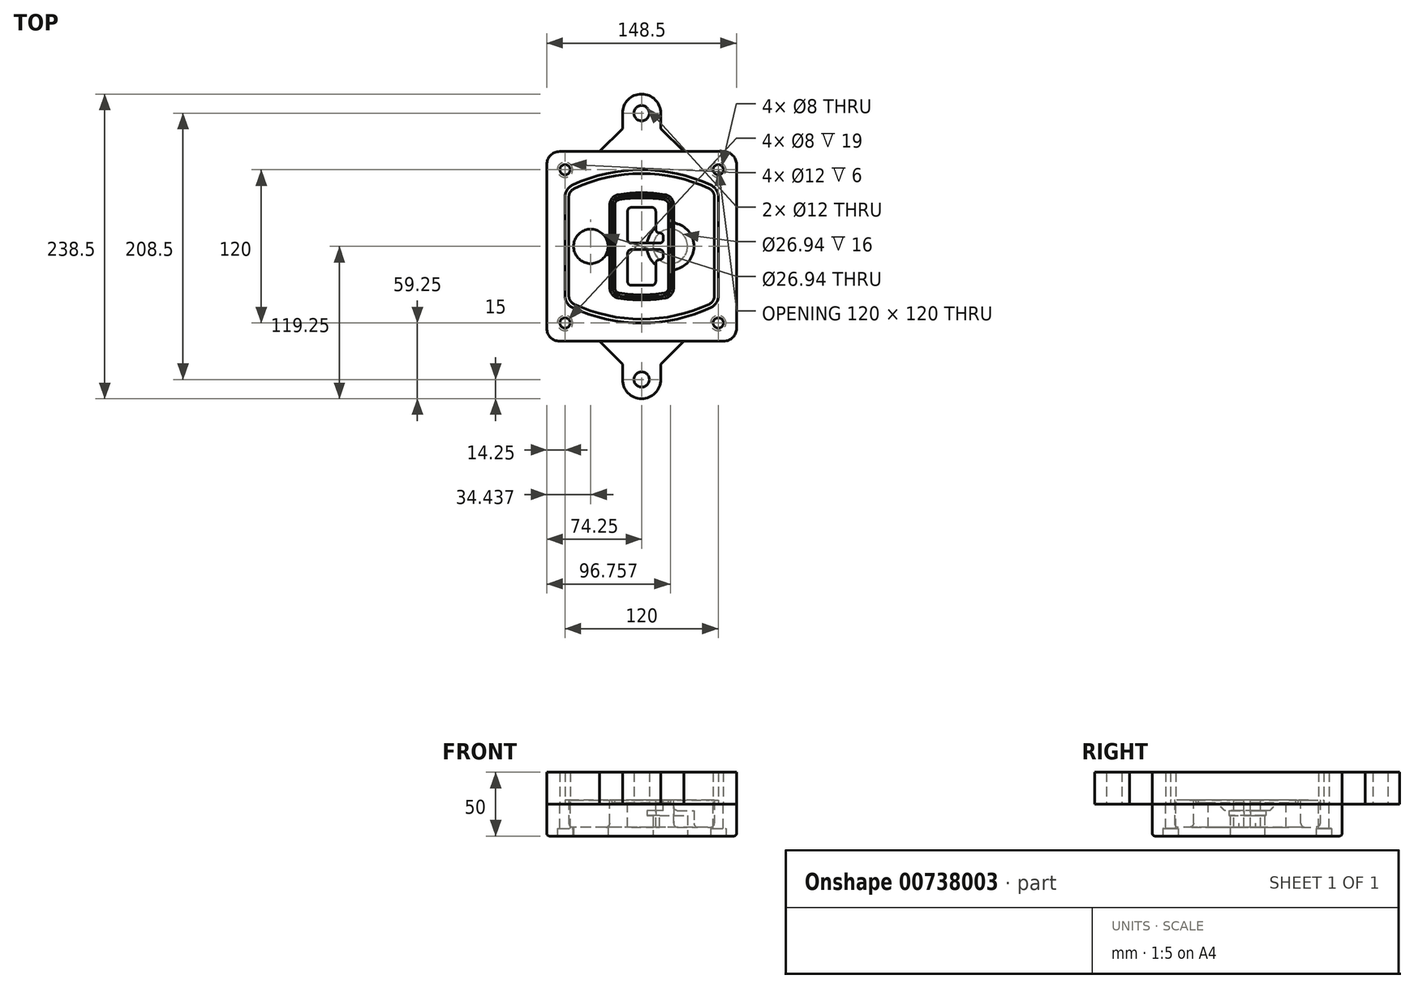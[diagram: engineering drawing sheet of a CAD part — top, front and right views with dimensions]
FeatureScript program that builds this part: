
annotation { "Feature Type Name" : "Feature", "Feature Type Description" : "" }
export const myFeature = defineFeature(function(context is Context, id is Id, definition is map)
    precondition{}
    {
        {
            var Q0;
            Q0=qCreatedBy(makeId("Top.planeOp"),FACE);
            var sketch = newSketch(context, id + "F0", { "sketchPlane" : qUnion([Q0])});
            skPoint(sketch, "E0.rect.middle", {"position": v(0, 0) * mm});
            skLineSegment(sketch, "E1.bottom", {"start": v(-64.25, -74.25) * mm, "end": v(64.25, -74.25) * mm});
            skLineSegment(sketch, "E1.top", {"start": v(-64.25, 74.25) * mm, "end": v(64.25, 74.25) * mm});
            skLineSegment(sketch, "E1.left", {"start": v(-74.25, -64.25) * mm, "end": v(-74.25, 64.25) * mm});
            skLineSegment(sketch, "E1.right", {"start": v(74.25, -64.25) * mm, "end": v(74.25, 64.25) * mm});
            skLineSegment(sketch, "E2", {"start": v(-74.25, 74.25) * mm, "end": v(74.25, -74.25) * mm, "construction": true});
            skLineSegment(sketch, "E3", {"start": v(74.25, 74.25) * mm, "end": v(-74.25, -74.25) * mm, "construction": true});
            skCircle(sketch, "E4", {"center": v(-60, 60) * mm, "radius": 4 * mm});
            skCircle(sketch, "E5", {"center": v(60, 60) * mm, "radius": 4 * mm});
            skCircle(sketch, "E6", {"center": v(60, -60) * mm, "radius": 4 * mm});
            skCircle(sketch, "E7", {"center": v(-60, -60) * mm, "radius": 4 * mm});
            skLineSegment(sketch, "E8", {"start": v(-60, 60) * mm, "end": v(60, 60) * mm, "construction": true});
            skLineSegment(sketch, "E9", {"start": v(60, 60) * mm, "end": v(60, -60) * mm, "construction": true});
            skLineSegment(sketch, "E10", {"start": v(60, -60) * mm, "end": v(-60, -60) * mm, "construction": true});
            skLineSegment(sketch, "E11", {"start": v(-60, -60) * mm, "end": v(-60, 60) * mm, "construction": true});
            skLineSegment(sketch, "E12", {"start": v(-60, 38.83) * mm, "end": v(-60, -38.83) * mm});
            skLineSegment(sketch, "E13", {"start": v(60, 38.83) * mm, "end": v(60, -38.83) * mm});
            skArc(sketch, "E14", {"start": v(54.26, 47.88) * mm, "mid": v(0, 60) * mm, "end": v(-54.26, 47.88) * mm});
            skArc(sketch, "E15", {"start": v(-54.26, -47.88) * mm, "mid": v(0, -60) * mm, "end": v(54.26, -47.88) * mm});
            skLineSegment(sketch, "E16", {"start": v(-60, 0) * mm, "end": v(60, 0) * mm, "construction": true});
            skPoint(sketch, "E17.visualSharp", {"position": v(-60, -45) * mm});
            skArc(sketch, "E17.filletArc", {"start": v(-60, -38.83) * mm, "mid": v(-58.44, -44.2) * mm, "end": v(-54.26, -47.88) * mm});
            skPoint(sketch, "E18.visualSharp", {"position": v(-60, 45) * mm});
            skArc(sketch, "E18.filletArc", {"start": v(-54.26, 47.88) * mm, "mid": v(-58.44, 44.2) * mm, "end": v(-60, 38.83) * mm});
            skPoint(sketch, "E19.visualSharp", {"position": v(60, 45) * mm});
            skArc(sketch, "E19.filletArc", {"start": v(60, 38.83) * mm, "mid": v(58.44, 44.2) * mm, "end": v(54.26, 47.88) * mm});
            skPoint(sketch, "E20.visualSharp", {"position": v(60, -45) * mm});
            skArc(sketch, "E20.filletArc", {"start": v(54.26, -47.88) * mm, "mid": v(58.44, -44.2) * mm, "end": v(60, -38.83) * mm});
            skPoint(sketch, "E21.visualSharp", {"position": v(-74.25, 74.25) * mm});
            skArc(sketch, "E21.filletArc", {"start": v(-64.25, 74.25) * mm, "mid": v(-71.32, 71.32) * mm, "end": v(-74.25, 64.25) * mm});
            skPoint(sketch, "E22.visualSharp", {"position": v(74.25, 74.25) * mm});
            skArc(sketch, "E22.filletArc", {"start": v(74.25, 64.25) * mm, "mid": v(71.32, 71.32) * mm, "end": v(64.25, 74.25) * mm});
            skPoint(sketch, "E23.visualSharp", {"position": v(74.25, -74.25) * mm});
            skArc(sketch, "E23.filletArc", {"start": v(64.25, -74.25) * mm, "mid": v(71.32, -71.32) * mm, "end": v(74.25, -64.25) * mm});
            skPoint(sketch, "E24.visualSharp", {"position": v(-74.25, -74.25) * mm});
            skArc(sketch, "E24.filletArc", {"start": v(-74.25, -64.25) * mm, "mid": v(-71.32, -71.32) * mm, "end": v(-64.25, -74.25) * mm});
            skArc(sketch, "E25.0", {"start": v(57, 38.83) * mm, "mid": v(55.9, 42.58) * mm, "end": v(52.98, 45.17) * mm});
            skLineSegment(sketch, "E25.1", {"start": v(57, 38.83) * mm, "end": v(57, -38.83) * mm});
            skArc(sketch, "E25.2", {"start": v(52.98, -45.17) * mm, "mid": v(55.9, -42.58) * mm, "end": v(57, -38.83) * mm});
            skArc(sketch, "E25.3", {"start": v(-52.98, -45.17) * mm, "mid": v(0, -57) * mm, "end": v(52.98, -45.17) * mm});
            skArc(sketch, "E25.4", {"start": v(-57, -38.83) * mm, "mid": v(-55.9, -42.58) * mm, "end": v(-52.98, -45.17) * mm});
            skArc(sketch, "E25.5", {"start": v(52.98, 45.17) * mm, "mid": v(0, 57) * mm, "end": v(-52.98, 45.17) * mm});
            skLineSegment(sketch, "E25.6", {"start": v(-57, 38.83) * mm, "end": v(-57, -38.83) * mm});
            skArc(sketch, "E25.7", {"start": v(-52.98, 45.17) * mm, "mid": v(-55.9, 42.58) * mm, "end": v(-57, 38.83) * mm});
            skArc(sketch, "E26.0", {"start": v(-55.96, 51.5) * mm, "mid": v(-61.82, 46.33) * mm, "end": v(-64, 38.83) * mm});
            skArc(sketch, "E26.1", {"start": v(55.96, 51.5) * mm, "mid": v(0, 64) * mm, "end": v(-55.96, 51.5) * mm});
            skArc(sketch, "E26.2", {"start": v(64, 38.83) * mm, "mid": v(61.82, 46.33) * mm, "end": v(55.96, 51.5) * mm});
            skLineSegment(sketch, "E26.3", {"start": v(64, 38.83) * mm, "end": v(64, -38.83) * mm});
            skArc(sketch, "E26.4", {"start": v(55.96, -51.5) * mm, "mid": v(61.82, -46.33) * mm, "end": v(64, -38.83) * mm});
            skLineSegment(sketch, "E26.5", {"start": v(-64, 38.83) * mm, "end": v(-64, -38.83) * mm});
            skArc(sketch, "E26.6", {"start": v(-55.96, -51.5) * mm, "mid": v(0, -64) * mm, "end": v(55.96, -51.5) * mm});
            skArc(sketch, "E26.7", {"start": v(-64, -38.83) * mm, "mid": v(-61.82, -46.33) * mm, "end": v(-55.96, -51.5) * mm});
            skSolve(sketch);
        }
        {
            var Q0;
            Q0=makeQuery(id+"F0.imprint","IMPRINT",FACE,{"disambiguationData":[TD([[makeQuery(id+"F0.imprint","IMPRINT",EDGE,{"derivedFrom":sQuery(id+"F0.wireOp",EDGE,"E1.bottom")}),1.0]])]});
            var Q1;
            Q1=makeQuery(id+"F0.imprint","IMPRINT",FACE,{"disambiguationData":[TD([[makeQuery(id+"F0.imprint","IMPRINT",EDGE,{"derivedFrom":sQuery(id+"F0.wireOp",EDGE,"E12")}),1.0]])]});
            var Q2;
            Q2=makeQuery(id+"F0.imprint","IMPRINT",FACE,{"disambiguationData":[TD([[makeQuery(id+"F0.imprint","IMPRINT",EDGE,{"derivedFrom":sQuery(id+"F0.wireOp",EDGE,"E25.0")}),1.0]])]});
            var Q3;
            Q3=makeQuery(id+"F0.imprint","IMPRINT",FACE,{"disambiguationData":[TD([[makeQuery(id+"F0.imprint","IMPRINT",EDGE,{"derivedFrom":sQuery(id+"F0.wireOp",EDGE,"E12")}),-1.0]])]});
            extrude(context, id + "F1", {"entities" : qUnion([Q0, Q1, Q2, Q3]), "oppositeDirection" : true, "depth" : 25 * mm});
        }
        {
            var Q0;
            Q0=makeQuery(id+"F0.imprint","IMPRINT",FACE,{"disambiguationData":[TD([[makeQuery(id+"F0.imprint","IMPRINT",EDGE,{"derivedFrom":sQuery(id+"F0.wireOp",EDGE,"E12")}),1.0]])]});
            extrude(context, id + "F2", {"entities" : qUnion([Q0]), "operationType" : NewBodyOperationType.ADD, "depth" : 3 * mm});
        }
        {
            var Q0;
            Q0=makeQuery(id+"F0.imprint","IMPRINT",FACE,{"disambiguationData":[TD([[makeQuery(id+"F0.imprint","IMPRINT",EDGE,{"derivedFrom":sQuery(id+"F0.wireOp",EDGE,"E25.0")}),1.0]])]});
            extrude(context, id + "F3", {"entities" : qUnion([Q0]), "operationType" : NewBodyOperationType.REMOVE, "oppositeDirection" : true, "depth" : 18 * mm});
        }
        {
            var Q0;
            Q0=makeQuery(id+"F2.opExtrude","CAP_FACE",FACE,{"disambiguationData":[OSD([sQuery(id+"F0.wireOp",EDGE,"E12"),sQuery(id+"F0.wireOp",EDGE,"E13"),sQuery(id+"F0.wireOp",EDGE,"E14"),sQuery(id+"F0.wireOp",EDGE,"E15"),sQuery(id+"F0.wireOp",EDGE,"E17.filletArc"),sQuery(id+"F0.wireOp",EDGE,"E18.filletArc"),sQuery(id+"F0.wireOp",EDGE,"E19.filletArc"),sQuery(id+"F0.wireOp",EDGE,"E20.filletArc"),sQuery(id+"F0.wireOp",EDGE,"E25.0"),sQuery(id+"F0.wireOp",EDGE,"E25.1"),sQuery(id+"F0.wireOp",EDGE,"E25.2"),sQuery(id+"F0.wireOp",EDGE,"E25.3"),sQuery(id+"F0.wireOp",EDGE,"E25.4"),sQuery(id+"F0.wireOp",EDGE,"E25.5"),sQuery(id+"F0.wireOp",EDGE,"E25.6"),sQuery(id+"F0.wireOp",EDGE,"E25.7")])],"isStart":false});
            var sketch = newSketch(context, id + "F4", { "sketchPlane" : qUnion([Q0])});
            skArc(sketch, "E27.0", {"start": v(-18.34, -40.45) * mm, "mid": v(0, -42) * mm, "end": v(18.34, -40.45) * mm});
            skArc(sketch, "E28.0", {"start": v(18.34, 40.45) * mm, "mid": v(0, 42) * mm, "end": v(-18.34, 40.45) * mm});
            skLineSegment(sketch, "E29", {"start": v(-25, 32.57) * mm, "end": v(-25, -32.57) * mm});
            skLineSegment(sketch, "E30", {"start": v(25, 32.57) * mm, "end": v(25, -32.57) * mm});
            skLineSegment(sketch, "E31", {"start": v(-25, 39.1) * mm, "end": v(25, 39.1) * mm, "construction": true});
            skLineSegment(sketch, "E32", {"start": v(-25, -39.1) * mm, "end": v(25, -39.1) * mm, "construction": true});
            skPoint(sketch, "E33.visualSharp", {"position": v(-25, 39.1) * mm});
            skArc(sketch, "E33.filletArc", {"start": v(-18.34, 40.45) * mm, "mid": v(-23.11, 37.73) * mm, "end": v(-25, 32.57) * mm});
            skPoint(sketch, "E34.visualSharp", {"position": v(25, 39.1) * mm});
            skArc(sketch, "E34.filletArc", {"start": v(25, 32.57) * mm, "mid": v(23.11, 37.73) * mm, "end": v(18.34, 40.45) * mm});
            skPoint(sketch, "E35.visualSharp", {"position": v(25, -39.1) * mm});
            skArc(sketch, "E35.filletArc", {"start": v(18.34, -40.45) * mm, "mid": v(23.11, -37.73) * mm, "end": v(25, -32.57) * mm});
            skPoint(sketch, "E36.visualSharp", {"position": v(-25, -39.1) * mm});
            skArc(sketch, "E36.filletArc", {"start": v(-25, -32.57) * mm, "mid": v(-23.11, -37.73) * mm, "end": v(-18.34, -40.45) * mm});
            skArc(sketch, "E37.0", {"start": v(52.98, 45.17) * mm, "mid": v(0, 57) * mm, "end": v(-52.98, 45.17) * mm});
            skArc(sketch, "E37.1", {"start": v(-52.98, 45.17) * mm, "mid": v(-55.9, 42.58) * mm, "end": v(-57, 38.83) * mm});
            skLineSegment(sketch, "E37.2", {"start": v(-57, 38.83) * mm, "end": v(-57, -38.83) * mm});
            skArc(sketch, "E37.3", {"start": v(-57, -38.83) * mm, "mid": v(-55.9, -42.58) * mm, "end": v(-52.98, -45.17) * mm});
            skArc(sketch, "E37.4", {"start": v(-52.98, -45.17) * mm, "mid": v(0, -57) * mm, "end": v(52.98, -45.17) * mm});
            skArc(sketch, "E37.5", {"start": v(52.98, -45.17) * mm, "mid": v(55.9, -42.58) * mm, "end": v(57, -38.83) * mm});
            skLineSegment(sketch, "E37.6", {"start": v(57, 38.83) * mm, "end": v(57, -38.83) * mm});
            skArc(sketch, "E37.7", {"start": v(57, 38.83) * mm, "mid": v(55.9, 42.58) * mm, "end": v(52.98, 45.17) * mm});
            skLineSegment(sketch, "E38.0", {"start": v(23, 32.57) * mm, "end": v(23, -32.57) * mm});
            skArc(sketch, "E38.1", {"start": v(18, -38.48) * mm, "mid": v(21.58, -36.44) * mm, "end": v(23, -32.57) * mm});
            skArc(sketch, "E38.2", {"start": v(-18, -38.48) * mm, "mid": v(0, -40) * mm, "end": v(18, -38.48) * mm});
            skArc(sketch, "E38.3", {"start": v(-23, -32.57) * mm, "mid": v(-21.58, -36.44) * mm, "end": v(-18, -38.48) * mm});
            skLineSegment(sketch, "E38.4", {"start": v(-23, 32.57) * mm, "end": v(-23, -32.57) * mm});
            skArc(sketch, "E38.5", {"start": v(23, 32.57) * mm, "mid": v(21.58, 36.44) * mm, "end": v(18, 38.48) * mm});
            skArc(sketch, "E38.6", {"start": v(-18, 38.48) * mm, "mid": v(-21.58, 36.44) * mm, "end": v(-23, 32.57) * mm});
            skArc(sketch, "E38.7", {"start": v(18, 38.48) * mm, "mid": v(0, 40) * mm, "end": v(-18, 38.48) * mm});
            skArc(sketch, "E39.0", {"start": v(21, 32.57) * mm, "mid": v(20.06, 35.15) * mm, "end": v(17.67, 36.5) * mm});
            skLineSegment(sketch, "E39.1", {"start": v(21, 32.57) * mm, "end": v(21, -32.57) * mm});
            skArc(sketch, "E39.2", {"start": v(17.67, -36.5) * mm, "mid": v(20.06, -35.15) * mm, "end": v(21, -32.57) * mm});
            skArc(sketch, "E39.3", {"start": v(-17.67, -36.5) * mm, "mid": v(0, -38) * mm, "end": v(17.67, -36.5) * mm});
            skArc(sketch, "E39.4", {"start": v(-21, -32.57) * mm, "mid": v(-20.06, -35.15) * mm, "end": v(-17.67, -36.5) * mm});
            skArc(sketch, "E39.5", {"start": v(17.67, 36.5) * mm, "mid": v(0, 38) * mm, "end": v(-17.67, 36.5) * mm});
            skLineSegment(sketch, "E39.6", {"start": v(-21, 32.57) * mm, "end": v(-21, -32.57) * mm});
            skArc(sketch, "E39.7", {"start": v(-17.67, 36.5) * mm, "mid": v(-20.06, 35.15) * mm, "end": v(-21, 32.57) * mm});
            skLineSegment(sketch, "E40", {"start": v(-25, 0) * mm, "end": v(25, 0) * mm, "construction": true});
            skLineSegment(sketch, "E41", {"start": v(-11, 5.5) * mm, "end": v(-11, 27.5) * mm});
            skLineSegment(sketch, "E42", {"start": v(-8, 30.5) * mm, "end": v(8, 30.5) * mm});
            skLineSegment(sketch, "E43", {"start": v(11, 27.5) * mm, "end": v(11, 13.5) * mm});
            skLineSegment(sketch, "E44", {"start": v(14, 10.5) * mm, "end": v(14, 10.5) * mm});
            skLineSegment(sketch, "E45", {"start": v(17, 7.5) * mm, "end": v(17, 5.5) * mm});
            skLineSegment(sketch, "E46", {"start": v(14, 2.5) * mm, "end": v(-8, 2.5) * mm});
            skPoint(sketch, "E47.visualSharp", {"position": v(-11, 30.5) * mm});
            skArc(sketch, "E47.filletArc", {"start": v(-8, 30.5) * mm, "mid": v(-10.12, 29.62) * mm, "end": v(-11, 27.5) * mm});
            skPoint(sketch, "E48.visualSharp", {"position": v(11, 30.5) * mm});
            skArc(sketch, "E48.filletArc", {"start": v(11, 27.5) * mm, "mid": v(10.12, 29.62) * mm, "end": v(8, 30.5) * mm});
            skPoint(sketch, "E49.visualSharp", {"position": v(11, 10.5) * mm});
            skArc(sketch, "E49.filletArc", {"start": v(11, 13.5) * mm, "mid": v(11.88, 11.38) * mm, "end": v(14, 10.5) * mm});
            skPoint(sketch, "E50.visualSharp", {"position": v(17, 10.5) * mm});
            skArc(sketch, "E50.filletArc", {"start": v(17, 7.5) * mm, "mid": v(16.12, 9.62) * mm, "end": v(14, 10.5) * mm});
            skPoint(sketch, "E51.visualSharp", {"position": v(17, 2.5) * mm});
            skArc(sketch, "E51.filletArc", {"start": v(14, 2.5) * mm, "mid": v(16.12, 3.38) * mm, "end": v(17, 5.5) * mm});
            skPoint(sketch, "E52.visualSharp", {"position": v(-11, 2.5) * mm});
            skArc(sketch, "E52.filletArc", {"start": v(-11, 5.5) * mm, "mid": v(-10.12, 3.38) * mm, "end": v(-8, 2.5) * mm});
            skLineSegment(sketch, "E53.0.MirrorCS", {"start": v(14, -2.5) * mm, "end": v(-8, -2.5) * mm});
            skArc(sketch, "E54.0.MirrorCS", {"start": v(-11, -5.5) * mm, "mid": v(-10.12, -3.38) * mm, "end": v(-8, -2.5) * mm});
            skLineSegment(sketch, "E55.0.MirrorCS", {"start": v(-11, -5.5) * mm, "end": v(-11, -27.5) * mm});
            skArc(sketch, "E56.0.MirrorCS", {"start": v(-8, -30.5) * mm, "mid": v(-10.12, -29.62) * mm, "end": v(-11, -27.5) * mm});
            skLineSegment(sketch, "E57.0.MirrorCS", {"start": v(-8, -30.5) * mm, "end": v(8, -30.5) * mm});
            skArc(sketch, "E58.0.MirrorCS", {"start": v(11, -27.5) * mm, "mid": v(10.12, -29.62) * mm, "end": v(8, -30.5) * mm});
            skLineSegment(sketch, "E59.0.MirrorCS", {"start": v(11, -27.5) * mm, "end": v(11, -13.5) * mm});
            skArc(sketch, "E60.0.MirrorCS", {"start": v(11, -13.5) * mm, "mid": v(11.88, -11.38) * mm, "end": v(14, -10.5) * mm});
            skArc(sketch, "E61.0.MirrorCS", {"start": v(17, -7.5) * mm, "mid": v(16.12, -9.62) * mm, "end": v(14, -10.5) * mm});
            skLineSegment(sketch, "E62.0.MirrorCS", {"start": v(17, -7.5) * mm, "end": v(17, -5.5) * mm});
            skArc(sketch, "E63.0.MirrorCS", {"start": v(14, -2.5) * mm, "mid": v(16.12, -3.38) * mm, "end": v(17, -5.5) * mm});
            skSolve(sketch);
        }
        {
            var Q0;
            Q0=makeQuery(id+"F4.imprint","IMPRINT",FACE,{"disambiguationData":[TD([[makeQuery(id+"F4.imprint","IMPRINT",EDGE,{"derivedFrom":sQuery(id+"F4.wireOp",EDGE,"E27.0")}),1.0]])]});
            var Q1;
            Q1=makeQuery(id+"F4.imprint","IMPRINT",FACE,{"disambiguationData":[TD([[makeQuery(id+"F4.imprint","IMPRINT",EDGE,{"derivedFrom":sQuery(id+"F4.wireOp",EDGE,"E38.0")}),-1.0]])]});
            var Q2;
            Q2=makeQuery(id+"F4.imprint","IMPRINT",FACE,{"disambiguationData":[TD([[makeQuery(id+"F4.imprint","IMPRINT",EDGE,{"derivedFrom":sQuery(id+"F4.wireOp",EDGE,"E39.0")}),1.0]])]});
            extrude(context, id + "F5", {"entities" : qUnion([Q0, Q1, Q2]), "operationType" : NewBodyOperationType.ADD, "endBound" : BoundingType.UP_TO_NEXT, "oppositeDirection" : true, "depth" : 25 * mm});
        }
        {
            var Q0;
            Q0=makeQuery(id+"F4.imprint","IMPRINT",FACE,{"disambiguationData":[TD([[makeQuery(id+"F4.imprint","IMPRINT",EDGE,{"derivedFrom":sQuery(id+"F4.wireOp",EDGE,"E38.0")}),-1.0]])]});
            extrude(context, id + "F6", {"entities" : qUnion([Q0]), "operationType" : NewBodyOperationType.REMOVE, "oppositeDirection" : true, "depth" : 2 * mm});
        }
        {
            var Q0;
            Q0=makeQuery(id+"F1.opExtrude","CAP_FACE",FACE,{"disambiguationData":[OSD([sQuery(id+"F0.wireOp",EDGE,"E1.bottom"),sQuery(id+"F0.wireOp",EDGE,"E1.top"),sQuery(id+"F0.wireOp",EDGE,"E1.left"),sQuery(id+"F0.wireOp",EDGE,"E1.right"),sQuery(id+"F0.wireOp",EDGE,"E4"),sQuery(id+"F0.wireOp",EDGE,"E5"),sQuery(id+"F0.wireOp",EDGE,"E6"),sQuery(id+"F0.wireOp",EDGE,"E7"),sQuery(id+"F0.wireOp",EDGE,"E21.filletArc"),sQuery(id+"F0.wireOp",EDGE,"E22.filletArc"),sQuery(id+"F0.wireOp",EDGE,"E23.filletArc"),sQuery(id+"F0.wireOp",EDGE,"E24.filletArc")])],"isStart":false});
            var sketch = newSketch(context, id + "F7", { "sketchPlane" : qUnion([Q0])});
            skCircle(sketch, "E64", {"center": v(22.5, 0) * mm, "radius": 13.47 * mm});
            skCircle(sketch, "E65", {"center": v(-39.81, 0) * mm, "radius": 13.47 * mm});
            skLineSegment(sketch, "E66", {"start": v(74.25, 0) * mm, "end": v(-74.25, 0) * mm});
            skCircle(sketch, "E67", {"center": v(22.5, 0) * mm, "radius": 18.47 * mm});
            skCircle(sketch, "E68", {"center": v(60, -60) * mm, "radius": 6 * mm});
            skCircle(sketch, "E69", {"center": v(-60, -60) * mm, "radius": 6 * mm});
            skCircle(sketch, "E70", {"center": v(-60, 60) * mm, "radius": 6 * mm});
            skCircle(sketch, "E71", {"center": v(60, 60) * mm, "radius": 6 * mm});
            skSolve(sketch);
        }
        {
            var Q0;
            {var subQ1=sQuery(id+"F7.wireOp",EDGE,"E66");var subQ4=sQuery(id+"F7.wireOp",EDGE,"E64");var subQ6=makeQuery(id+"F7.imprint","INTERSECT",VERTEX,{"disambiguationData":[OD(0.0)],"derivedFrom":[subQ4,subQ1]});Q0=makeQuery(id+"F7.imprint","IMPRINT",FACE,{"disambiguationData":[TD([[makeQuery(id+"F7.imprint","IMPRINT",EDGE,{"disambiguationData":[TD([[subQ6,-1.0]])],"derivedFrom":subQ4}),-1.0]])]});}
            var Q1;
            {var subQ0=sQuery(id+"F7.wireOp",EDGE,"E66");var subQ1=sQuery(id+"F7.wireOp",EDGE,"E64");var subQ3=makeQuery(id+"F7.imprint","INTERSECT",VERTEX,{"disambiguationData":[OD(0.0)],"derivedFrom":[subQ1,subQ0]});Q1=makeQuery(id+"F7.imprint","IMPRINT",FACE,{"disambiguationData":[TD([[makeQuery(id+"F7.imprint","IMPRINT",EDGE,{"disambiguationData":[TD([[subQ3,-1.0]])],"derivedFrom":subQ1}),1.0]])]});}
            var Q2;
            {var subQ0=sQuery(id+"F7.wireOp",EDGE,"E66");var subQ1=sQuery(id+"F7.wireOp",EDGE,"E64");var subQ3=makeQuery(id+"F7.imprint","INTERSECT",VERTEX,{"disambiguationData":[OD(0.0)],"derivedFrom":[subQ1,subQ0]});Q2=makeQuery(id+"F7.imprint","IMPRINT",FACE,{"disambiguationData":[TD([[makeQuery(id+"F7.imprint","IMPRINT",EDGE,{"disambiguationData":[TD([[subQ3,1.0]])],"derivedFrom":subQ1}),1.0]])]});}
            var Q3;
            {var subQ1=sQuery(id+"F7.wireOp",EDGE,"E66");var subQ4=sQuery(id+"F7.wireOp",EDGE,"E64");var subQ6=makeQuery(id+"F7.imprint","INTERSECT",VERTEX,{"disambiguationData":[OD(0.0)],"derivedFrom":[subQ4,subQ1]});Q3=makeQuery(id+"F7.imprint","IMPRINT",FACE,{"disambiguationData":[TD([[makeQuery(id+"F7.imprint","IMPRINT",EDGE,{"disambiguationData":[TD([[subQ6,1.0]])],"derivedFrom":subQ4}),-1.0]])]});}
            extrude(context, id + "F8", {"entities" : qUnion([Q0, Q1, Q2, Q3]), "operationType" : NewBodyOperationType.ADD, "oppositeDirection" : true, "depth" : 20 * mm});
        }
        {
            var Q0;
            {var subQ0=sQuery(id+"F7.wireOp",EDGE,"E66");var subQ1=sQuery(id+"F7.wireOp",EDGE,"E64");var subQ3=makeQuery(id+"F7.imprint","INTERSECT",VERTEX,{"disambiguationData":[OD(0.0)],"derivedFrom":[subQ1,subQ0]});Q0=makeQuery(id+"F7.imprint","IMPRINT",FACE,{"disambiguationData":[TD([[makeQuery(id+"F7.imprint","IMPRINT",EDGE,{"disambiguationData":[TD([[subQ3,-1.0]])],"derivedFrom":subQ1}),1.0]])]});}
            var Q1;
            {var subQ0=sQuery(id+"F7.wireOp",EDGE,"E66");var subQ1=sQuery(id+"F7.wireOp",EDGE,"E64");var subQ3=makeQuery(id+"F7.imprint","INTERSECT",VERTEX,{"disambiguationData":[OD(0.0)],"derivedFrom":[subQ1,subQ0]});Q1=makeQuery(id+"F7.imprint","IMPRINT",FACE,{"disambiguationData":[TD([[makeQuery(id+"F7.imprint","IMPRINT",EDGE,{"disambiguationData":[TD([[subQ3,1.0]])],"derivedFrom":subQ1}),1.0]])]});}
            extrude(context, id + "F9", {"entities" : qUnion([Q0, Q1]), "operationType" : NewBodyOperationType.REMOVE, "oppositeDirection" : true, "depth" : 16 * mm});
        }
        {
            var Q0;
            {var subQ0=sQuery(id+"F7.wireOp",EDGE,"E66");var subQ1=sQuery(id+"F7.wireOp",EDGE,"E65");var subQ3=makeQuery(id+"F7.imprint","INTERSECT",VERTEX,{"disambiguationData":[OD(0.0)],"derivedFrom":[subQ1,subQ0]});Q0=makeQuery(id+"F7.imprint","IMPRINT",FACE,{"disambiguationData":[TD([[makeQuery(id+"F7.imprint","IMPRINT",EDGE,{"disambiguationData":[TD([[subQ3,-1.0]])],"derivedFrom":subQ1}),1.0]])]});}
            var Q1;
            {var subQ0=sQuery(id+"F7.wireOp",EDGE,"E66");var subQ1=sQuery(id+"F7.wireOp",EDGE,"E65");var subQ3=makeQuery(id+"F7.imprint","INTERSECT",VERTEX,{"disambiguationData":[OD(0.0)],"derivedFrom":[subQ1,subQ0]});Q1=makeQuery(id+"F7.imprint","IMPRINT",FACE,{"disambiguationData":[TD([[makeQuery(id+"F7.imprint","IMPRINT",EDGE,{"disambiguationData":[TD([[subQ3,1.0]])],"derivedFrom":subQ1}),1.0]])]});}
            extrude(context, id + "F10", {"entities" : qUnion([Q0, Q1]), "operationType" : NewBodyOperationType.REMOVE, "oppositeDirection" : true, "depth" : 25 * mm});
        }
        {
            var Q0;
            Q0=makeQuery(id+"F7.imprint","IMPRINT",FACE,{"disambiguationData":[TD([[makeQuery(id+"F7.imprint","IMPRINT",EDGE,{"derivedFrom":sQuery(id+"F7.wireOp",EDGE,"E68")}),1.0]])]});
            var Q1;
            Q1=makeQuery(id+"F7.imprint","IMPRINT",FACE,{"disambiguationData":[TD([[makeQuery(id+"F7.imprint","IMPRINT",EDGE,{"derivedFrom":makeQuery(id+"F1.opExtrude","CAP_EDGE",EDGE,{"disambiguationData":[OSD([sQuery(id+"F0.wireOp",EDGE,"E5")])],"isStart":false})}),-1.0]])]});
            var Q2;
            Q2=makeQuery(id+"F7.imprint","IMPRINT",FACE,{"disambiguationData":[TD([[makeQuery(id+"F7.imprint","IMPRINT",EDGE,{"derivedFrom":sQuery(id+"F7.wireOp",EDGE,"E69")}),1.0]])]});
            var Q3;
            Q3=makeQuery(id+"F7.imprint","IMPRINT",FACE,{"disambiguationData":[TD([[makeQuery(id+"F7.imprint","IMPRINT",EDGE,{"derivedFrom":makeQuery(id+"F1.opExtrude","CAP_EDGE",EDGE,{"disambiguationData":[OSD([sQuery(id+"F0.wireOp",EDGE,"E4")])],"isStart":false})}),-1.0]])]});
            var Q4;
            Q4=makeQuery(id+"F7.imprint","IMPRINT",FACE,{"disambiguationData":[TD([[makeQuery(id+"F7.imprint","IMPRINT",EDGE,{"derivedFrom":sQuery(id+"F7.wireOp",EDGE,"E70")}),1.0]])]});
            var Q5;
            Q5=makeQuery(id+"F7.imprint","IMPRINT",FACE,{"disambiguationData":[TD([[makeQuery(id+"F7.imprint","IMPRINT",EDGE,{"derivedFrom":makeQuery(id+"F1.opExtrude","CAP_EDGE",EDGE,{"disambiguationData":[OSD([sQuery(id+"F0.wireOp",EDGE,"E7")])],"isStart":false})}),-1.0]])]});
            var Q6;
            Q6=makeQuery(id+"F7.imprint","IMPRINT",FACE,{"disambiguationData":[TD([[makeQuery(id+"F7.imprint","IMPRINT",EDGE,{"derivedFrom":sQuery(id+"F7.wireOp",EDGE,"E71")}),1.0]])]});
            var Q7;
            Q7=makeQuery(id+"F7.imprint","IMPRINT",FACE,{"disambiguationData":[TD([[makeQuery(id+"F7.imprint","IMPRINT",EDGE,{"derivedFrom":makeQuery(id+"F1.opExtrude","CAP_EDGE",EDGE,{"disambiguationData":[OSD([sQuery(id+"F0.wireOp",EDGE,"E6")])],"isStart":false})}),-1.0]])]});
            extrude(context, id + "F11", {"entities" : qUnion([Q0, Q1, Q2, Q3, Q4, Q5, Q6, Q7]), "operationType" : NewBodyOperationType.REMOVE, "oppositeDirection" : true, "depth" : 6 * mm});
        }
        {
            var Q0;
            Q0=makeQuery(id+"F9.boolean.opBoolean","COPY",FACE,{"derivedFrom":makeQuery(id+"F9.opExtrude","CAP_FACE",FACE,{"disambiguationData":[OSD([sQuery(id+"F7.wireOp",EDGE,"E64")])],"isStart":false})});
            var sketch = newSketch(context, id + "F12", { "sketchPlane" : qUnion([Q0])});
            skArc(sketch, "E72.0", {"start": v(11, 14.45) * mm, "mid": v(6.45, 9.13) * mm, "end": v(4.2, 2.5) * mm});
            skArc(sketch, "E72.1", {"start": v(4.2, -2.5) * mm, "mid": v(6.45, -9.13) * mm, "end": v(11, -14.45) * mm});
            skLineSegment(sketch, "E73", {"start": v(4.2, -2.5) * mm, "end": v(14, -2.5) * mm});
            skLineSegment(sketch, "E74.0", {"start": v(14, 2.5) * mm, "end": v(4.2, 2.5) * mm});
            skArc(sketch, "E74.1", {"start": v(14, 2.5) * mm, "mid": v(16.12, 3.38) * mm, "end": v(17, 5.5) * mm});
            skLineSegment(sketch, "E74.2", {"start": v(17, 7.5) * mm, "end": v(17, 5.5) * mm});
            skArc(sketch, "E74.3", {"start": v(17, 7.5) * mm, "mid": v(16.12, 9.62) * mm, "end": v(14, 10.5) * mm});
            skArc(sketch, "E74.4", {"start": v(11, 13.5) * mm, "mid": v(11.88, 11.38) * mm, "end": v(14, 10.5) * mm});
            skLineSegment(sketch, "E74.5", {"start": v(11, 14.45) * mm, "end": v(11, 13.5) * mm});
            skLineSegment(sketch, "E74.7", {"start": v(14, -2.5) * mm, "end": v(4.2, -2.5) * mm});
            skArc(sketch, "E74.8", {"start": v(14, -2.5) * mm, "mid": v(16.12, -3.38) * mm, "end": v(17, -5.5) * mm});
            skLineSegment(sketch, "E74.9", {"start": v(17, -7.5) * mm, "end": v(17, -5.5) * mm});
            skArc(sketch, "E74.10", {"start": v(17, -7.5) * mm, "mid": v(16.12, -9.62) * mm, "end": v(14, -10.5) * mm});
            skArc(sketch, "E74.11", {"start": v(11, -13.5) * mm, "mid": v(11.88, -11.38) * mm, "end": v(14, -10.5) * mm});
            skLineSegment(sketch, "E74.12", {"start": v(11, -14.45) * mm, "end": v(11, -13.5) * mm});
            skPoint(sketch, "E75.orphan", {"position": v(11, -27.5) * mm});
            skPoint(sketch, "E76.orphan", {"position": v(-8, -2.5) * mm});
            skPoint(sketch, "E77.orphan", {"position": v(-8, 2.5) * mm});
            skPoint(sketch, "E78.orphan", {"position": v(11, 27.5) * mm});
            skSolve(sketch);
        }
        {
            var Q0;
            {var subQ7=sQuery(id+"F12.wireOp",EDGE,"E72.0");var subQ14=sQuery(id+"F12.wireOp",EDGE,"E72.1");var subQ16=sQuery(id+"F12.wireOp",EDGE,"E74.1");var subQ18=sQuery(id+"F12.wireOp",EDGE,"E74.8");Q0=qUnion([makeQuery(id+"F12.imprint","IMPRINT",FACE,{"disambiguationData":[TD([[makeQuery(id+"F12.imprint","IMPRINT",EDGE,{"derivedFrom":subQ7}),1.0]])]}),makeQuery(id+"F12.imprint","IMPRINT",FACE,{"disambiguationData":[TD([[makeQuery(id+"F12.imprint","IMPRINT",EDGE,{"derivedFrom":subQ14}),1.0]])]}),makeQuery(id+"F12.imprint","IMPRINT",FACE,{"disambiguationData":[TD([[makeQuery(id+"F12.imprint","IMPRINT",EDGE,{"derivedFrom":subQ16}),1.0]])]}),makeQuery(id+"F12.imprint","IMPRINT",FACE,{"disambiguationData":[TD([[makeQuery(id+"F12.imprint","IMPRINT",EDGE,{"derivedFrom":subQ18}),-1.0]])]})]);}
            var Q1;
            Q1=makeQuery(id+"F5.boolean.opBoolean","SPLIT",FACE,{"disambiguationData":[TD([makeQuery(id+"F5.opExtrude","SWEPT_FACE",FACE,{"disambiguationData":[OSD([sQuery(id+"F4.wireOp",EDGE,"E41")])]})])],"derivedFrom":makeQuery(id+"F3.boolean.opBoolean","COPY",FACE,{"derivedFrom":makeQuery(id+"F3.opExtrude","CAP_FACE",FACE,{"disambiguationData":[OSD([sQuery(id+"F0.wireOp",EDGE,"E25.0"),sQuery(id+"F0.wireOp",EDGE,"E25.1"),sQuery(id+"F0.wireOp",EDGE,"E25.2"),sQuery(id+"F0.wireOp",EDGE,"E25.3"),sQuery(id+"F0.wireOp",EDGE,"E25.4"),sQuery(id+"F0.wireOp",EDGE,"E25.5"),sQuery(id+"F0.wireOp",EDGE,"E25.6"),sQuery(id+"F0.wireOp",EDGE,"E25.7")])],"isStart":false})})});
            extrude(context, id + "F13", {"entities" : qUnion([Q0]), "operationType" : NewBodyOperationType.REMOVE, "endBound" : BoundingType.UP_TO_SURFACE, "endBoundEntityFace" : qUnion([Q1]), "depth" : 25 * mm});
        }
        {
            var Q0;
            Q0=makeQuery(id+"F3.boolean.opBoolean","COPY",EDGE,{"derivedFrom":makeQuery(id+"F3.opExtrude","CAP_EDGE",EDGE,{"disambiguationData":[OSD([sQuery(id+"F0.wireOp",EDGE,"E25.6")])],"isStart":false})});
            var Q1;
            Q1=makeQuery(id+"F8.boolean.opBoolean","INTERSECT",EDGE,{"derivedFrom":[makeQuery(id+"F5.opExtrude","SWEPT_FACE",FACE,{"disambiguationData":[OSD([sQuery(id+"F4.wireOp",EDGE,"E30")])]}),makeQuery(id+"F8.opExtrude","CAP_FACE",FACE,{"disambiguationData":[OSD([sQuery(id+"F7.wireOp",EDGE,"E67")])],"isStart":false})]});
            var Q2;
            Q2=makeQuery(id+"F8.boolean.opBoolean","INTERSECT",EDGE,{"disambiguationData":[OD(1.0)],"derivedFrom":[makeQuery(id+"F5.opExtrude","SWEPT_FACE",FACE,{"disambiguationData":[OSD([sQuery(id+"F4.wireOp",EDGE,"E30")])]}),makeQuery(id+"F8.opExtrude","SWEPT_FACE",FACE,{"disambiguationData":[OSD([sQuery(id+"F7.wireOp",EDGE,"E67")])]})]});
            var Q3;
            {var subQ0=sQuery(id+"F4.wireOp",EDGE,"E30");Q3=makeQuery(id+"F8.boolean.opBoolean","SPLIT",EDGE,{"disambiguationData":[TD([makeQuery(id+"F5.opExtrude","SWEPT_FACE",FACE,{"disambiguationData":[OSD([sQuery(id+"F4.wireOp",EDGE,"E35.filletArc")])]})])],"derivedFrom":makeQuery(id+"F5.opExtrude","CAP_EDGE",EDGE,{"disambiguationData":[OSD([subQ0])],"isStart":false})});}
            var Q4;
            {var subQ0=sQuery(id+"F0.wireOp",EDGE,"E25.7");var subQ1=sQuery(id+"F0.wireOp",EDGE,"E25.1");var subQ2=sQuery(id+"F0.wireOp",EDGE,"E25.6");var subQ3=sQuery(id+"F0.wireOp",EDGE,"E25.5");var subQ4=sQuery(id+"F0.wireOp",EDGE,"E25.4");var subQ5=sQuery(id+"F0.wireOp",EDGE,"E25.0");var subQ6=sQuery(id+"F0.wireOp",EDGE,"E25.2");var subQ7=sQuery(id+"F0.wireOp",EDGE,"E25.3");Q4=makeQuery(id+"F8.boolean.opBoolean","INTERSECT",EDGE,{"derivedFrom":[makeQuery(id+"F5.boolean.opBoolean","SPLIT",FACE,{"disambiguationData":[TD([makeQuery(id+"F2.opExtrude","SWEPT_FACE",FACE,{"disambiguationData":[OSD([subQ5])]})])],"derivedFrom":makeQuery(id+"F3.boolean.opBoolean","COPY",FACE,{"derivedFrom":makeQuery(id+"F3.opExtrude","CAP_FACE",FACE,{"disambiguationData":[OSD([subQ5,subQ1,subQ6,subQ7,subQ4,subQ3,subQ2,subQ0])],"isStart":false})})}),makeQuery(id+"F8.opExtrude","SWEPT_FACE",FACE,{"disambiguationData":[OSD([sQuery(id+"F7.wireOp",EDGE,"E67")])]})]});}
            var Q5;
            Q5=makeQuery(id+"F8.boolean.opBoolean","INTERSECT",EDGE,{"disambiguationData":[OD(0.0)],"derivedFrom":[makeQuery(id+"F5.opExtrude","SWEPT_FACE",FACE,{"disambiguationData":[OSD([sQuery(id+"F4.wireOp",EDGE,"E30")])]}),makeQuery(id+"F8.opExtrude","SWEPT_FACE",FACE,{"disambiguationData":[OSD([sQuery(id+"F7.wireOp",EDGE,"E67")])]})]});
            fillet(context, id + "F14", {"entities" : qUnion([Q0, Q1, Q2, Q3, Q4, Q5]), "radius" : 3 * mm, "tangentPropagation" : true, "allowEdgeOverflow" : false});
        }
        {
            var Q0;
            Q0=makeQuery(id+"F1.opExtrude","CAP_EDGE",EDGE,{"disambiguationData":[OSD([sQuery(id+"F0.wireOp",EDGE,"E1.bottom")])],"isStart":false});
            fillet(context, id + "F15", {"entities" : qUnion([Q0]), "radius" : 2 * mm, "tangentPropagation" : true, "allowEdgeOverflow" : false});
        }
        {
            var Q0;
            {var subQ0=sQuery(id+"F0.wireOp",EDGE,"E21.filletArc");var subQ1=sQuery(id+"F0.wireOp",EDGE,"E7");var subQ2=sQuery(id+"F0.wireOp",EDGE,"E6");var subQ3=sQuery(id+"F0.wireOp",EDGE,"E5");var subQ4=sQuery(id+"F0.wireOp",EDGE,"E4");var subQ5=sQuery(id+"F0.wireOp",EDGE,"E22.filletArc");var subQ6=sQuery(id+"F0.wireOp",EDGE,"E1.bottom");var subQ7=sQuery(id+"F0.wireOp",EDGE,"E1.right");var subQ8=sQuery(id+"F0.wireOp",EDGE,"E1.top");var subQ9=sQuery(id+"F0.wireOp",EDGE,"E1.left");var subQ10=sQuery(id+"F0.wireOp",EDGE,"E23.filletArc");var subQ11=sQuery(id+"F0.wireOp",EDGE,"E24.filletArc");Q0=makeQuery(id+"F2.boolean.opBoolean","SPLIT",FACE,{"disambiguationData":[TD([makeQuery(id+"F1.opExtrude","SWEPT_FACE",FACE,{"disambiguationData":[OSD([subQ6])]})])],"derivedFrom":makeQuery(id+"F1.opExtrude","CAP_FACE",FACE,{"disambiguationData":[OSD([subQ6,subQ8,subQ9,subQ7,subQ4,subQ3,subQ2,subQ1,subQ0,subQ5,subQ10,subQ11])],"isStart":true})});}
            var sketch = newSketch(context, id + "F16", { "sketchPlane" : qUnion([Q0])});
            skLineSegment(sketch, "E79", {"start": v(0, 74.25) * mm, "end": v(0, 104.25) * mm, "construction": true});
            skCircle(sketch, "E80", {"center": v(0, 104.25) * mm, "radius": 6 * mm});
            skLineSegment(sketch, "E81", {"start": v(-33, 74.25) * mm, "end": v(-15, 92.25) * mm});
            skLineSegment(sketch, "E82", {"start": v(-15, 92.25) * mm, "end": v(-15, 104.25) * mm});
            skLineSegment(sketch, "E83", {"start": v(33, 74.25) * mm, "end": v(15, 92.25) * mm});
            skLineSegment(sketch, "E84", {"start": v(15, 92.25) * mm, "end": v(15, 104.25) * mm});
            skArc(sketch, "E85", {"start": v(15, 104.25) * mm, "mid": v(0, 119.25) * mm, "end": v(-15, 104.25) * mm});
            skLineSegment(sketch, "E86", {"start": v(-74.25, 0) * mm, "end": v(74.25, 0) * mm, "construction": true});
            skLineSegment(sketch, "E87.MirrorCS", {"start": v(15, -92.25) * mm, "end": v(15, -104.25) * mm});
            skLineSegment(sketch, "E88.MirrorCS", {"start": v(-33, -74.25) * mm, "end": v(33, -74.25) * mm});
            skArc(sketch, "E89.MirrorCS", {"start": v(15, -104.25) * mm, "mid": v(0, -119.25) * mm, "end": v(-15, -104.25) * mm});
            skLineSegment(sketch, "E90.MirrorCS", {"start": v(33, -74.25) * mm, "end": v(15, -92.25) * mm});
            skCircle(sketch, "E91.MirrorC", {"center": v(0, -104.25) * mm, "radius": 6 * mm});
            skLineSegment(sketch, "E92.MirrorCS", {"start": v(-33, -74.25) * mm, "end": v(-15, -92.25) * mm});
            skLineSegment(sketch, "E93.MirrorCS", {"start": v(0, -74.25) * mm, "end": v(0, -104.25) * mm, "construction": true});
            skLineSegment(sketch, "E94.MirrorCS", {"start": v(-15, -92.25) * mm, "end": v(-15, -104.25) * mm});
            skSolve(sketch);
        }
        {
            var Q0;
            Q0=makeQuery(id+"F16.imprint","IMPRINT",FACE,{"disambiguationData":[TD([[makeQuery(id+"F16.imprint","IMPRINT",EDGE,{"derivedFrom":sQuery(id+"F16.wireOp",EDGE,"E80")}),-1.0]])]});
            var Q1;
            Q1=makeQuery(id+"F16.imprint","IMPRINT",FACE,{"disambiguationData":[TD([[makeQuery(id+"F16.imprint","IMPRINT",EDGE,{"derivedFrom":sQuery(id+"F16.wireOp",EDGE,"E87.MirrorCS")}),-1.0]])]});
            extrude(context, id + "F17", {"entities" : qUnion([Q0, Q1]), "depth" : 25 * mm, "offsetDistance" : 25 * mm});
        }
        {
            var Q0;
            {var subQ0=sQuery(id+"F0.wireOp",EDGE,"E21.filletArc");var subQ1=sQuery(id+"F0.wireOp",EDGE,"E7");var subQ2=sQuery(id+"F0.wireOp",EDGE,"E6");var subQ3=sQuery(id+"F0.wireOp",EDGE,"E5");var subQ4=sQuery(id+"F0.wireOp",EDGE,"E4");var subQ5=sQuery(id+"F0.wireOp",EDGE,"E22.filletArc");var subQ6=sQuery(id+"F0.wireOp",EDGE,"E1.bottom");var subQ7=sQuery(id+"F0.wireOp",EDGE,"E1.right");var subQ8=sQuery(id+"F0.wireOp",EDGE,"E1.top");var subQ9=sQuery(id+"F0.wireOp",EDGE,"E1.left");var subQ10=sQuery(id+"F0.wireOp",EDGE,"E23.filletArc");var subQ11=sQuery(id+"F0.wireOp",EDGE,"E24.filletArc");Q0=makeQuery(id+"F2.boolean.opBoolean","SPLIT",FACE,{"disambiguationData":[TD([makeQuery(id+"F1.opExtrude","SWEPT_FACE",FACE,{"disambiguationData":[OSD([subQ6])]})])],"derivedFrom":makeQuery(id+"F1.opExtrude","CAP_FACE",FACE,{"disambiguationData":[OSD([subQ6,subQ8,subQ9,subQ7,subQ4,subQ3,subQ2,subQ1,subQ0,subQ5,subQ10,subQ11])],"isStart":true})});}
            extrude(context, id + "F18", {"entities" : qUnion([Q0]), "depth" : 25 * mm, "offsetDistance" : 25 * mm});
        }
    });
